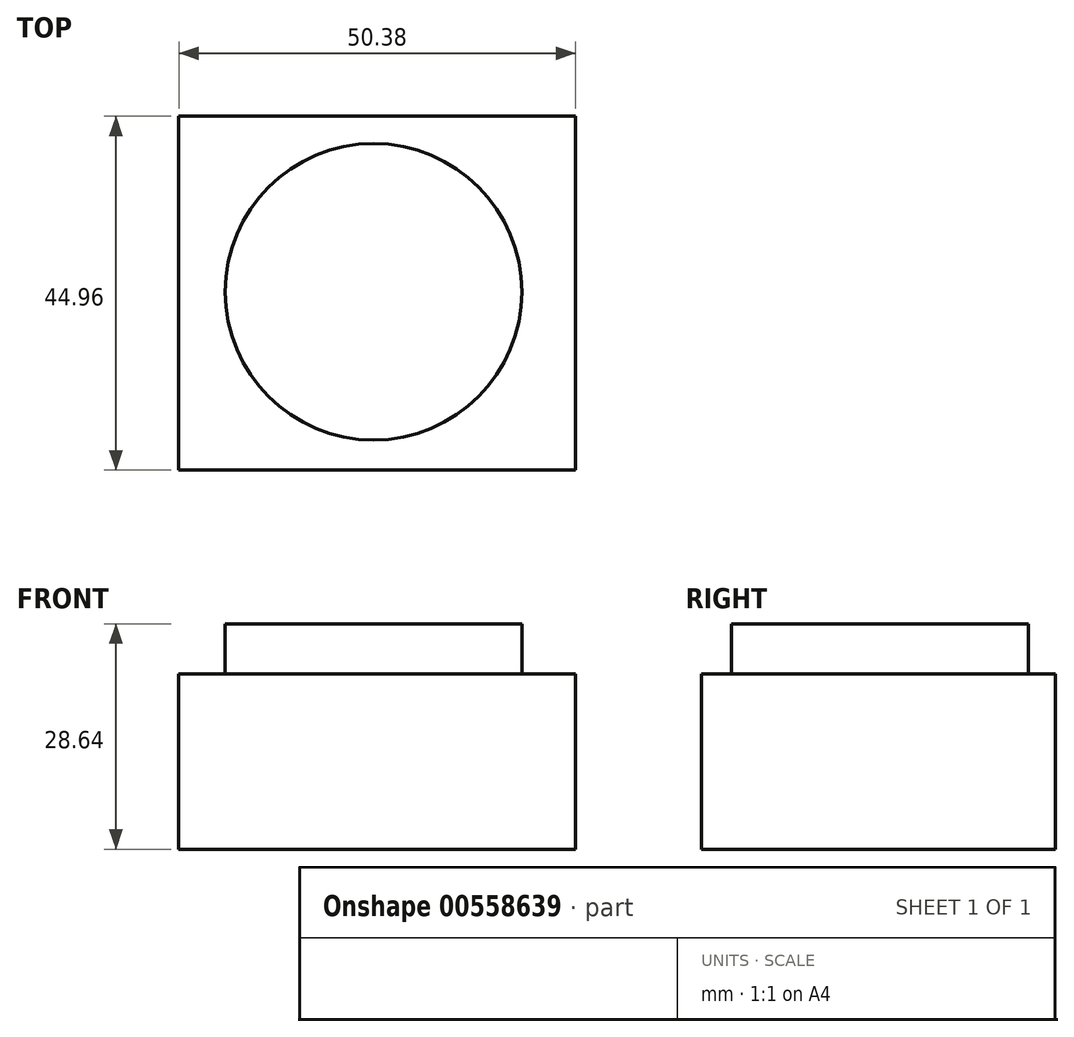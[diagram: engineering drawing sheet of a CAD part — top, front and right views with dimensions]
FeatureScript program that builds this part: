
annotation { "Feature Type Name" : "Feature", "Feature Type Description" : "" }
export const myFeature = defineFeature(function(context is Context, id is Id, definition is map)
    precondition{}
    {
        {
            var Q0;
            Q0=qCreatedBy(makeId("Front.planeOp"),FACE);
            var sketch = newSketch(context, id + "F0", { "sketchPlane" : qUnion([Q0])});
            skLineSegment(sketch, "E0.bottom", {"start": v(-15.57, 10.69) * mm, "end": v(34.81, 10.69) * mm});
            skLineSegment(sketch, "E0.top", {"start": v(-15.57, -11.6) * mm, "end": v(34.81, -11.6) * mm});
            skLineSegment(sketch, "E0.left", {"start": v(-15.57, 10.69) * mm, "end": v(-15.57, -11.6) * mm});
            skLineSegment(sketch, "E0.right", {"start": v(34.81, 10.69) * mm, "end": v(34.81, -11.6) * mm});
            skSolve(sketch);
        }
        {
            var Q0;
            Q0 = qSketchRegion(id + "F0", true);
            extrude(context, id + "F1", {"entities" : qUnion([Q0]), "depth" : 44.96 * mm, "offsetDistance" : 25.4 * mm});
        }
        {
            var Q0;
            Q0=makeQuery(id+"F1.opExtrude","SWEPT_FACE",FACE,{"disambiguationData":[OSD([sQuery(id+"F0.wireOp",EDGE,"E0.bottom")])]});
            var sketch = newSketch(context, id + "F2", { "sketchPlane" : qUnion([Q0])});
            skCircle(sketch, "E1", {"center": v(9.16, -22.3) * mm, "radius": 18.84 * mm});
            skSolve(sketch);
        }
        {
            var Q0;
            Q0 = qSketchRegion(id + "F2", true);
            extrude(context, id + "F3", {"entities" : qUnion([Q0]), "operationType" : NewBodyOperationType.ADD, "depth" : 6.35 * mm, "offsetDistance" : 25.4 * mm});
        }
    });
